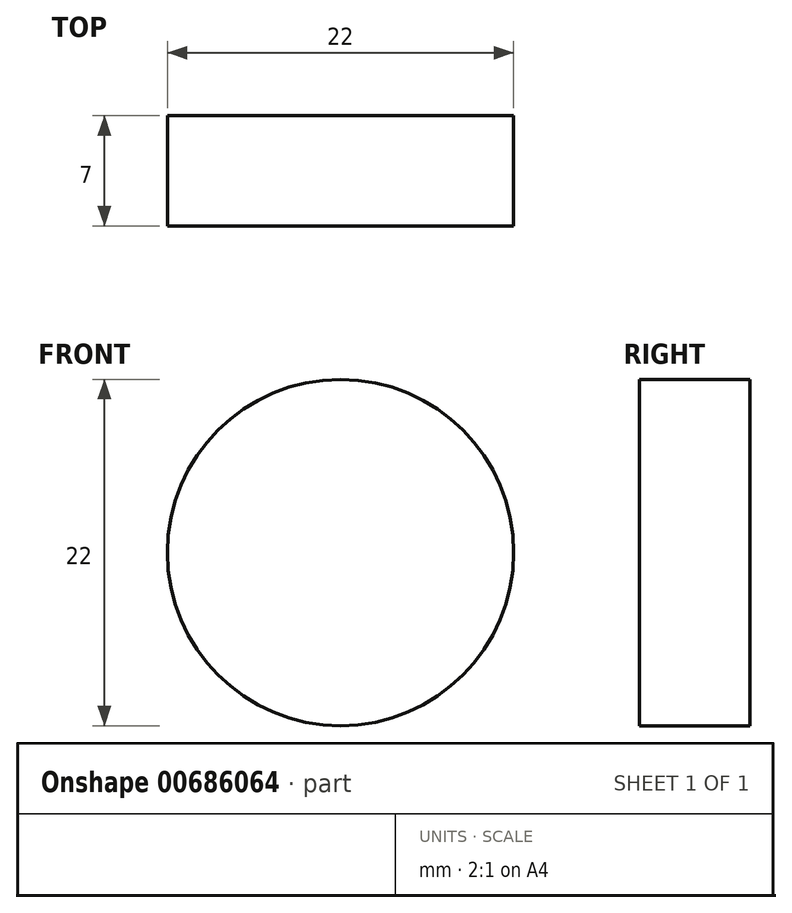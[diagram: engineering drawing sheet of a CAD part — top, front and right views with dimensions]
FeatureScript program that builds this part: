
annotation { "Feature Type Name" : "Feature", "Feature Type Description" : "" }
export const myFeature = defineFeature(function(context is Context, id is Id, definition is map)
    precondition{}
    {
        {
            var Q0;
            Q0=qCreatedBy(makeId("Front.planeOp"),FACE);
            var sketch = newSketch(context, id + "F0", { "sketchPlane" : qUnion([Q0])});
            skCircle(sketch, "E0", {"center": v(0, -1.53) * mm, "radius": 11 * mm});
            skSolve(sketch);
        }
        {
            var Q0;
            Q0=makeQuery(id+"F0.imprint","IMPRINT",FACE,{"disambiguationData":[TD([[makeQuery(id+"F0.imprint","IMPRINT",EDGE,{"derivedFrom":sQuery(id+"F0.wireOp",EDGE,"E0")}),1.0]])]});
            extrude(context, id + "F1", {"entities" : qUnion([Q0]), "depth" : 7 * mm, "offsetDistance" : 25 * mm});
        }
    });
